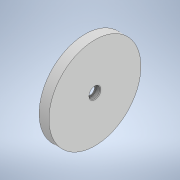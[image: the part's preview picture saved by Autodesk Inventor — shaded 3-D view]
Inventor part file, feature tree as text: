
AUTODESK INVENTOR PART (.ipt)
format: ipt  version: 2020 (Build 240168000, 168)  size: 153,600 bytes
history: native  units: mm
features: revolve x1, chamfer x1, sketch x1
ambient origin geometry x8: Origin, YZ Plane, XZ Plane, XY Plane, X Axis, Y Axis, Z Axis, Center Point
bodies: Solid1 (feature_tree)
feature tree (3):
  revolve  "Revolution1"  [1 undecoded]
  chamfer  "Chamfer1"  Angle=90.0deg  [1 undecoded]
  sketch  "Sketch1"  dims[d6=69.57767mm d7=8.5mm d11=90.0deg d15=1.5mm d17=6.0mm d18=1.625mm d19=1.0mm d20=2.0mm d21=45.0deg d22=7.0mm d23=1.0mm d24=3.0mm d25=64.0mm d26=4.0mm d27=15.0mm]
note: 2 required parameter values undecoded (feature->parameter linkage not recoverable at this tier; creation-order binding heuristic only, values carry confidence <= 0.55)